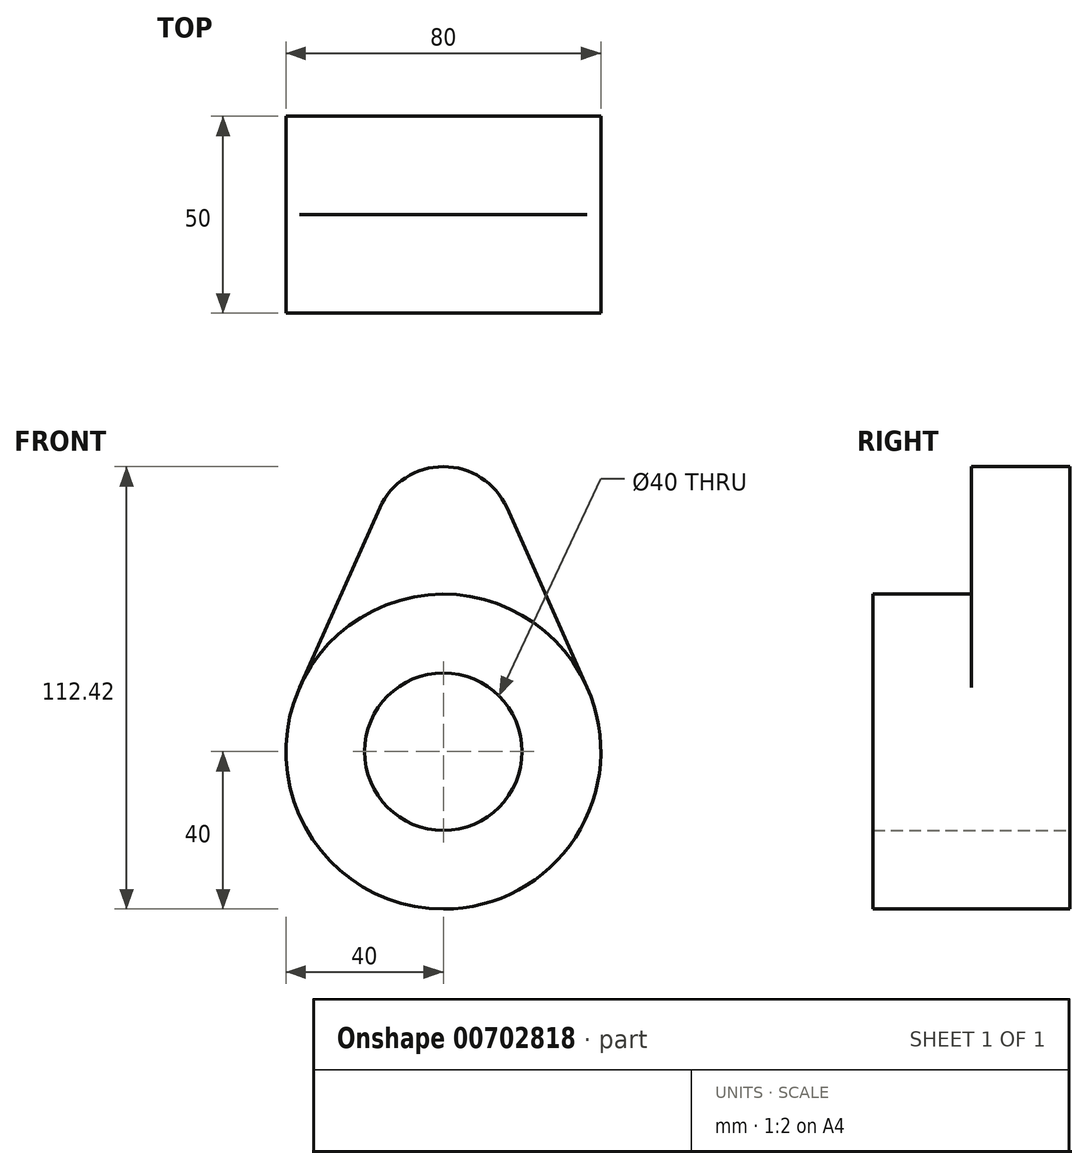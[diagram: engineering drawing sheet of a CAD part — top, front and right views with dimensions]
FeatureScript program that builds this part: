
annotation { "Feature Type Name" : "Feature", "Feature Type Description" : "" }
export const myFeature = defineFeature(function(context is Context, id is Id, definition is map)
    precondition{}
    {
        {
            var Q0;
            Q0=qCreatedBy(makeId("Front.planeOp"),FACE);
            var sketch = newSketch(context, id + "F0", { "sketchPlane" : qUnion([Q0])});
            skCircle(sketch, "E0", {"center": v(0, 0) * mm, "radius": 20 * mm});
            skCircle(sketch, "E1", {"center": v(0, 0) * mm, "radius": 40 * mm});
            skLineSegment(sketch, "E2", {"start": v(-36.52, 16.32) * mm, "end": v(-16.12, 61.97) * mm});
            skLineSegment(sketch, "E3", {"start": v(36.52, 16.32) * mm, "end": v(16.12, 61.97) * mm});
            skArc(sketch, "E4", {"start": v(16.12, 61.97) * mm, "mid": v(0, 72.42) * mm, "end": v(-16.12, 61.97) * mm});
            skSolve(sketch);
        }
        {
            var Q0;
            Q0=makeQuery(id+"F0.imprint","IMPRINT",FACE,{"disambiguationData":[TD([[makeQuery(id+"F0.imprint","IMPRINT",EDGE,{"derivedFrom":sQuery(id+"F0.wireOp",EDGE,"E0")}),-1.0]])]});
            extrude(context, id + "F1", {"entities" : qUnion([Q0]), "depth" : 50 * mm, "offsetDistance" : 25 * mm});
        }
        {
            var Q0;
            {var subQ0=sQuery(id+"F0.wireOp",EDGE,"E2");Q0=makeQuery(id+"F0.imprint","IMPRINT",FACE,{"disambiguationData":[TD([[makeQuery(id+"F0.imprint","IMPRINT",EDGE,{"derivedFrom":subQ0}),-1.0]])]});}
            extrude(context, id + "F2", {"entities" : qUnion([Q0]), "operationType" : NewBodyOperationType.ADD, "depth" : 25 * mm, "offsetDistance" : 25 * mm});
        }
    });
